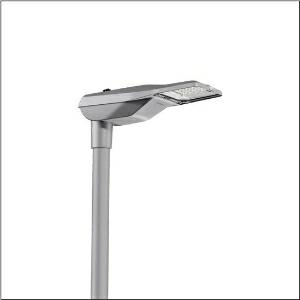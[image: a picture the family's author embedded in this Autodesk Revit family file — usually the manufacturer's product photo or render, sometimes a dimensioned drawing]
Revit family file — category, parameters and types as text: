
# Revit family: streetlight_sl_21_iq_micro___st1_0ab_5xe1m31v08db_4fb3
name_source: partatom
category: Lighting Fixtures
units: mm (PartAtom-declared; Revit-internal decimal feet)

## family parameters
Cut with Voids When Loaded = No
Host = Face
Light Source = No
Part Type = Normal
Room Calculation Point = No
Round Connector Dimension = Use Diameter
Shared = No

## types (1)
- --- (1 x LED, 4490 lm, 39.1 W, 3000K)
    Apparent Load = 39 VA
    CIE Flux Codes = 38 73 97 100 100
    Color Rendering = 70
    Color Temperature = 3000K
    Default Elevation = 1800 mm
    Description = Streetlight SL 21 iQ micro, mast luminaire, primary light control with lens, of PMMA, primary optical cover: cover, of toughened safety glass, transparent, light distribution: ST1.0aB, light emission: direct distribution, primary light characteristic: asymmetric, installation type: post-top, side-entry, LED, High Power LED, rated luminous flux: 4.490lm, luminous efficacy: 115lm/W, light colour: 730, colour temperature: 3000K, control gear: iQ-Street Remote, D4i with power reduction, control: pre-setting: logarithmic dimming characteristic, Street-Remote, Auto-Match, Temp-Guard, Lumen-Switch, Night-Set, Smart-Wire, Light-Fading, Desk-Remote (wireless, voltage-free reading and setting of iQ features in the workshop via application-optimized NFC function/RFID function), optimised constant luminous flux control (CLO 2.0), mains connection: 220..240V, AC, 50/60Hz, start of lifetime: 39W, end of service life: 41W, reduction: 17W, luminaire housing, of diecast aluminium, powder-coated, SITECO metallic grey (DB 702S), corrosivity category C5 high according to DIN EN ISO 12944, please order mast flange separately, inclination adjustable: 0°, 5°, 10°, 15°, sealing non-destructively replaceable, multi-level sealing system, length: 528mm, width: 235mm, height: 110mm, mast flange for spigot size: 42mm (side-entry): 5XC10008XM4, 60/48mm (side-entry/post-top): 5XC10108XM2, 76/60mm (side-entry/post-top): 5XC10108XM1, mounting height: 4..8m, Smart Interface above, protection rating (complete): IP66, insulation class (complete): insulation class II (safety insulation), certification: CE, ENEC, ENEC+, VDE, impact resistance: IK10, permissible operating ambient temperature for outdoor applications: -40..+50°C, standard-compliant lighting for roads and squares, packaging unit: 1 piece

Light Distribution: ST1.0aB
    Height = 110 mm
    Lamp = 1 x LED
    Lamp Light Flux = 4490 lm
    Lamp Power = 39.1 W
    Lamp count = 1
    Length = 528 mm
    Luminous efficacy = 115 lm/W
    Manufacturer = Siteco
    ModVariant = No
    Model = 5XE1M31V08DB
    Number of Poles = 1
    OnlyDefault = Yes
    Power Factor = 1
    Product Name = Streetlight SL 21 iQ micro | ST1.0aB
    Product group = mast luminaire | pylon top
    ProductGroupID = 6100
    Protection Class = Protection class II
    Protection Degree = IP 66
    RLX_Detail_Level = 1
    RLX_Emergency_Light_Flux = 0 lm
    RLX_Emergency_Type = 0
    RLX_Emergency_Type_DB = No
    RlxData = <blob elided: 98309 chars, md5=745520ac>
    Socket = socket
    Standby Power = 0 W
    System Light Flux = 4490 lm
    System Power = 39 W
    Type Comments = factory setting: luminous flux: 100 % | dim-lin: 254 | 765 mA
    Type Image = l_1277292.jpg
    URL = http://relux.com
    VarID = @adj_112701
    Voltage = 0 V
    Weight = 0.00 kg
    Width = 235 mm

## geometry (parser evidence)
native form markers: Blend x4, Sweep x11
no freeform markers — native parametric forms only
